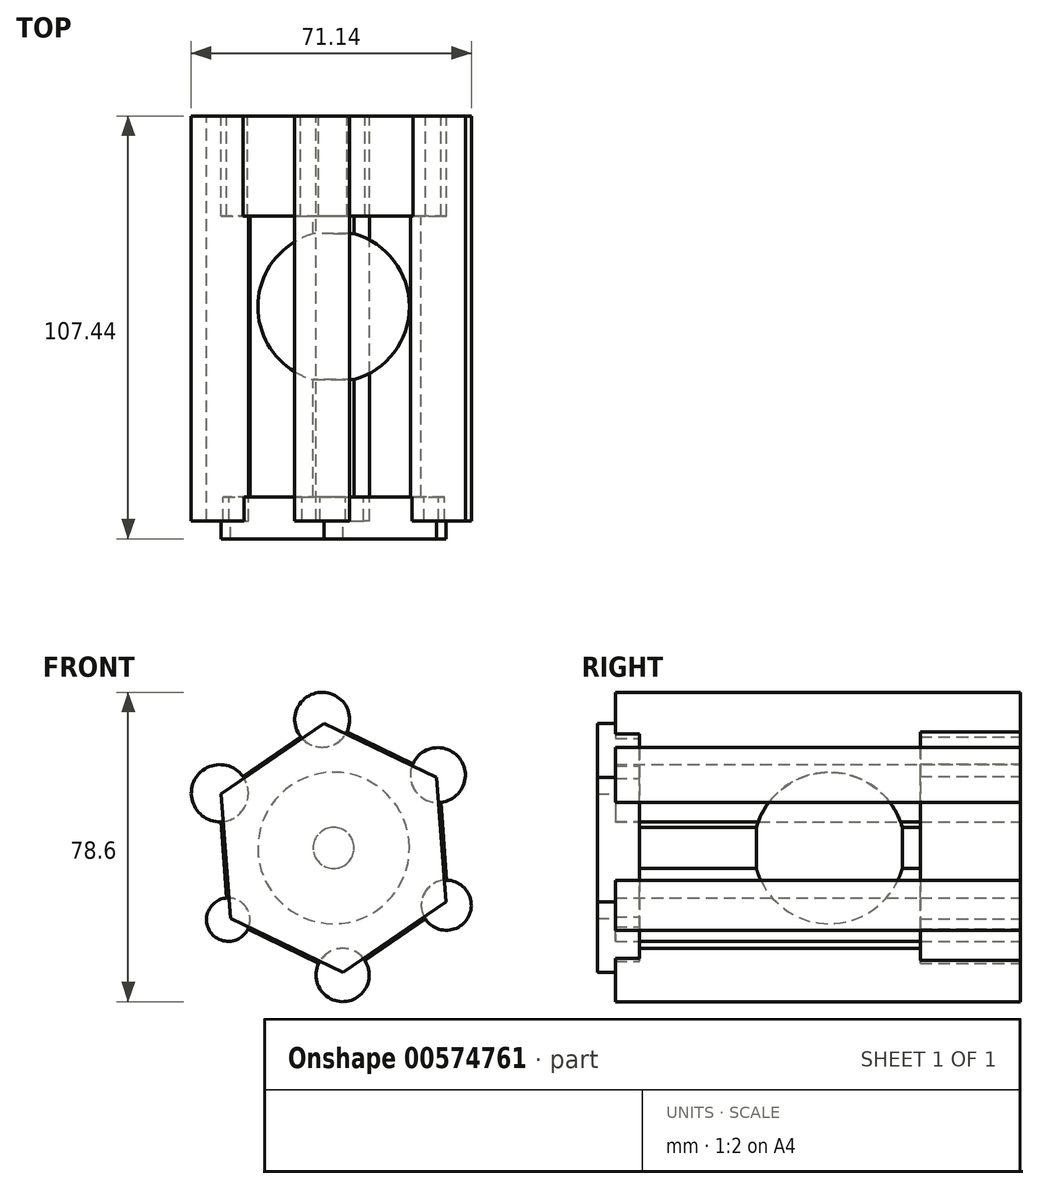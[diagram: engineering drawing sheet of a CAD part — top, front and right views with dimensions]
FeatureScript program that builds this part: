
annotation { "Feature Type Name" : "Feature", "Feature Type Description" : "" }
export const myFeature = defineFeature(function(context is Context, id is Id, definition is map)
    precondition{}
    {
        {
            var Q0;
            Q0=qCreatedBy(makeId("Front.planeOp"),FACE);
            var sketch = newSketch(context, id + "F0", { "sketchPlane" : qUnion([Q0])});
            skCircle(sketch, "E0.cCircle", {"center": v(0, 0) * mm, "radius": 32.38 * mm, "construction": true});
            skLineSegment(sketch, "E0.0", {"start": v(-26.77, -18.2) * mm, "end": v(-29.15, 14.08) * mm});
            skLineSegment(sketch, "E0.1", {"start": v(-29.15, 14.08) * mm, "end": v(-2.38, 32.29) * mm});
            skLineSegment(sketch, "E0.2", {"start": v(-2.38, 32.29) * mm, "end": v(26.77, 18.2) * mm});
            skLineSegment(sketch, "E0.3", {"start": v(26.77, 18.2) * mm, "end": v(29.15, -14.08) * mm});
            skLineSegment(sketch, "E0.4", {"start": v(29.15, -14.08) * mm, "end": v(2.38, -32.29) * mm});
            skLineSegment(sketch, "E0.5", {"start": v(2.38, -32.29) * mm, "end": v(-26.77, -18.2) * mm});
            skSolve(sketch);
        }
        {
            var Q0;
            Q0 = qSketchRegion(id + "F0", true);
            extrude(context, id + "F1", {"entities" : qUnion([Q0]), "depth" : 25.4 * mm, "offsetDistance" : 25.4 * mm});
        }
        {
            var Q0;
            Q0=qCreatedBy(makeId("Front.planeOp"),FACE);
            var sketch = newSketch(context, id + "F2", { "sketchPlane" : qUnion([Q0])});
            skCircle(sketch, "E1", {"center": v(-28.91, 13.92) * mm, "radius": 7.25 * mm});
            skCircle(sketch, "E2", {"center": v(-26.77, -18.2) * mm, "radius": 5.52 * mm});
            skCircle(sketch, "E3", {"center": v(2.3, -32.28) * mm, "radius": 6.76 * mm});
            skCircle(sketch, "E4", {"center": v(28.6, -14.53) * mm, "radius": 6.37 * mm});
            skCircle(sketch, "E5", {"center": v(26.47, 18.51) * mm, "radius": 6.98 * mm});
            skCircle(sketch, "E6", {"center": v(-2.9, 32.59) * mm, "radius": 6.98 * mm});
            skSolve(sketch);
        }
        {
            var Q0;
            Q0 = qSketchRegion(id + "F2", true);
            extrude(context, id + "F3", {"entities" : qUnion([Q0]), "operationType" : NewBodyOperationType.ADD, "depth" : 102.87 * mm, "offsetDistance" : 25.4 * mm});
        }
        {
            var Q0;
            Q0=qCreatedBy(makeId("Front.planeOp"),FACE);
            var sketch = newSketch(context, id + "F4", { "sketchPlane" : qUnion([Q0])});
            skCircle(sketch, "E7", {"center": v(0, 0) * mm, "radius": 5.2 * mm});
            skSolve(sketch);
        }
        {
            var Q0;
            Q0 = qSketchRegion(id + "F4", true);
            extrude(context, id + "F5", {"entities" : qUnion([Q0]), "operationType" : NewBodyOperationType.ADD, "depth" : 102.1 * mm, "offsetDistance" : 25.4 * mm});
        }
        {
            var Q0;
            Q0=qCreatedBy(makeId("Top.planeOp"),FACE);
            var sketch = newSketch(context, id + "F6", { "sketchPlane" : qUnion([Q0])});
            skArc(sketch, "E8", {"start": v(0, -29.23) * mm, "mid": v(-19.25, -48.48) * mm, "end": v(0, -67.72) * mm});
            skLineSegment(sketch, "E9", {"start": v(0, -29.23) * mm, "end": v(0, -67.72) * mm});
            skSolve(sketch);
        }
        {
            var Q0;
            Q0 = qSketchRegion(id + "F6", true);
            var Q1;
            Q1=sQuery(id+"F6.wireOp",EDGE,"E9");
            revolve(context, id + "F7", {"operationType" : NewBodyOperationType.ADD, "entities" : qUnion([Q0]), "axis" : qUnion([Q1]), "revolveType" : RevolveType.FULL});
        }
        {
            var Q0;
            Q0=qCreatedBy(makeId("Front.planeOp"),FACE);
            var sketch = newSketch(context, id + "F8", { "sketchPlane" : qUnion([Q0])});
            skCircle(sketch, "E10.cCircle", {"center": v(0, 0) * mm, "radius": 31.7 * mm, "construction": true});
            skLineSegment(sketch, "E10.0", {"start": v(-26.16, -17.9) * mm, "end": v(-28.58, 13.7) * mm});
            skLineSegment(sketch, "E10.1", {"start": v(-28.58, 13.7) * mm, "end": v(-2.42, 31.6) * mm});
            skLineSegment(sketch, "E10.2", {"start": v(-2.42, 31.6) * mm, "end": v(26.16, 17.9) * mm});
            skLineSegment(sketch, "E10.3", {"start": v(26.16, 17.9) * mm, "end": v(28.58, -13.7) * mm});
            skLineSegment(sketch, "E10.4", {"start": v(28.58, -13.7) * mm, "end": v(2.42, -31.6) * mm});
            skLineSegment(sketch, "E10.5", {"start": v(2.42, -31.6) * mm, "end": v(-26.16, -17.9) * mm});
            skSolve(sketch);
        }
        {
            var Q0;
            Q0 = qSketchRegion(id + "F8", true);
            extrude(context, id + "F9", {"entities" : qUnion([Q0]), "operationType" : NewBodyOperationType.ADD, "depth" : 107.44 * mm, "offsetDistance" : 25.4 * mm, "hasSecondDirection" : true, "secondDirectionOppositeDirection" : false, "secondDirectionDepth" : 96.77 * mm});
        }
    });
